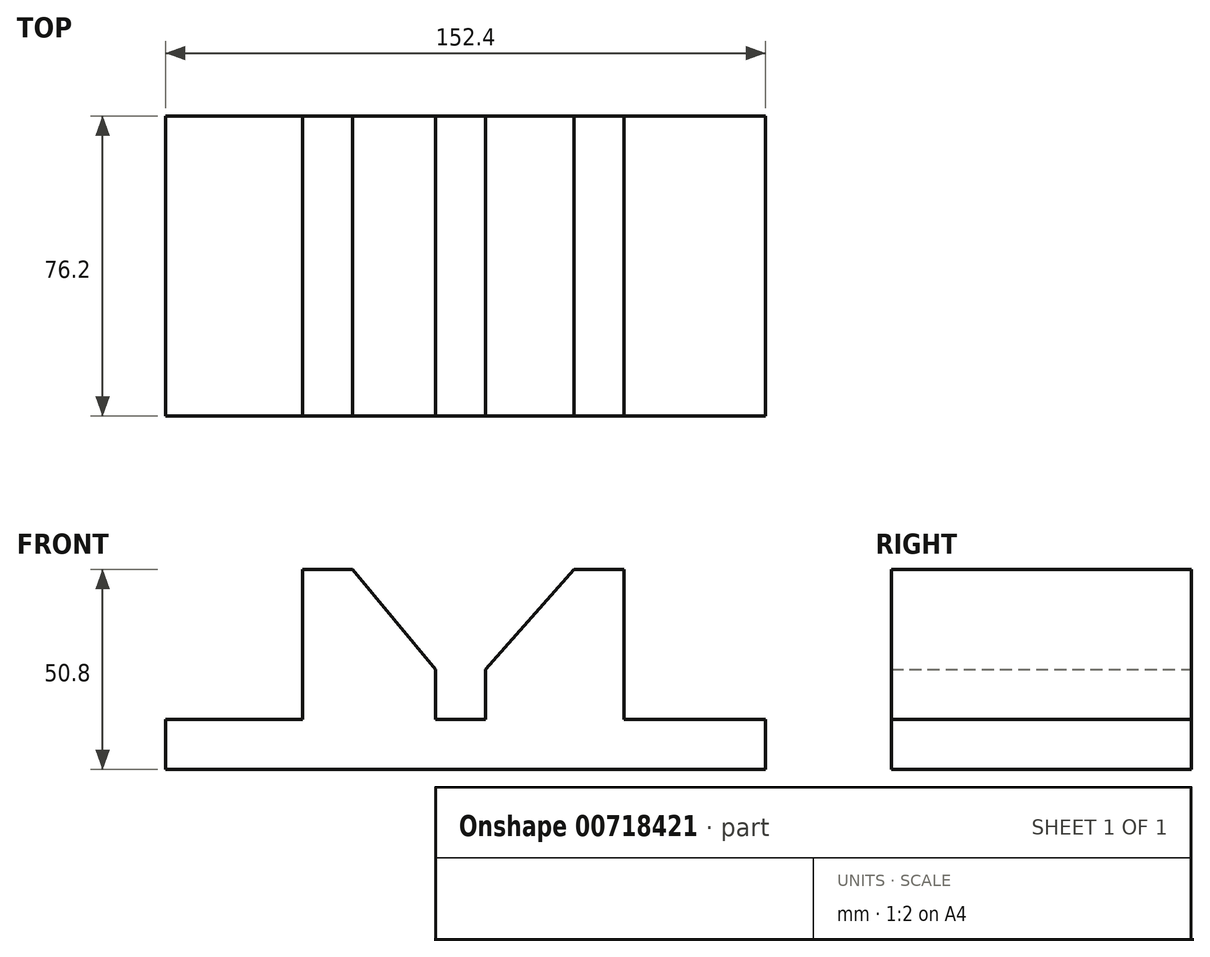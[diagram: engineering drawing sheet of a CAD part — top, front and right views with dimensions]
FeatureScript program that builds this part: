
annotation { "Feature Type Name" : "Feature", "Feature Type Description" : "" }
export const myFeature = defineFeature(function(context is Context, id is Id, definition is map)
    precondition{}
    {
        {
            var Q0;
            Q0=qCreatedBy(makeId("Front.planeOp"),FACE);
            var sketch = newSketch(context, id + "F0", { "sketchPlane" : qUnion([Q0])});
            skLineSegment(sketch, "E0", {"start": v(-79.23, -50.14) * mm, "end": v(73.17, -50.14) * mm});
            skLineSegment(sketch, "E1", {"start": v(73.17, -50.14) * mm, "end": v(73.17, -37.44) * mm});
            skLineSegment(sketch, "E2", {"start": v(73.17, -37.44) * mm, "end": v(37.25, -37.44) * mm});
            skLineSegment(sketch, "E3", {"start": v(37.25, -37.44) * mm, "end": v(37.25, 0.66) * mm});
            skLineSegment(sketch, "E4", {"start": v(37.25, 0.66) * mm, "end": v(24.55, 0.66) * mm});
            skLineSegment(sketch, "E5", {"start": v(24.55, 0.66) * mm, "end": v(2.08, -24.74) * mm});
            skLineSegment(sketch, "E6", {"start": v(2.08, -24.74) * mm, "end": v(2.08, -37.44) * mm});
            skLineSegment(sketch, "E7", {"start": v(2.08, -37.44) * mm, "end": v(-10.62, -37.44) * mm});
            skLineSegment(sketch, "E8", {"start": v(-10.62, -37.44) * mm, "end": v(-10.62, -24.74) * mm});
            skLineSegment(sketch, "E9", {"start": v(-10.62, -24.74) * mm, "end": v(-31.69, 0.66) * mm});
            skLineSegment(sketch, "E10", {"start": v(-31.69, 0.66) * mm, "end": v(-44.39, 0.66) * mm});
            skLineSegment(sketch, "E11", {"start": v(-44.39, 0.66) * mm, "end": v(-44.39, -37.44) * mm});
            skLineSegment(sketch, "E12", {"start": v(-44.39, -37.44) * mm, "end": v(-79.23, -37.44) * mm});
            skLineSegment(sketch, "E13", {"start": v(-79.23, -37.44) * mm, "end": v(-79.23, -50.14) * mm});
            skSolve(sketch);
        }
        {
            var Q0;
            Q0=makeQuery(id+"F0.imprint","IMPRINT",FACE,{"disambiguationData":[TD([[makeQuery(id+"F0.imprint","IMPRINT",EDGE,{"derivedFrom":sQuery(id+"F0.wireOp",EDGE,"E0")}),1.0]])]});
            extrude(context, id + "F1", {"entities" : qUnion([Q0]), "depth" : 76.2 * mm, "offsetDistance" : 25.4 * mm});
        }
    });
